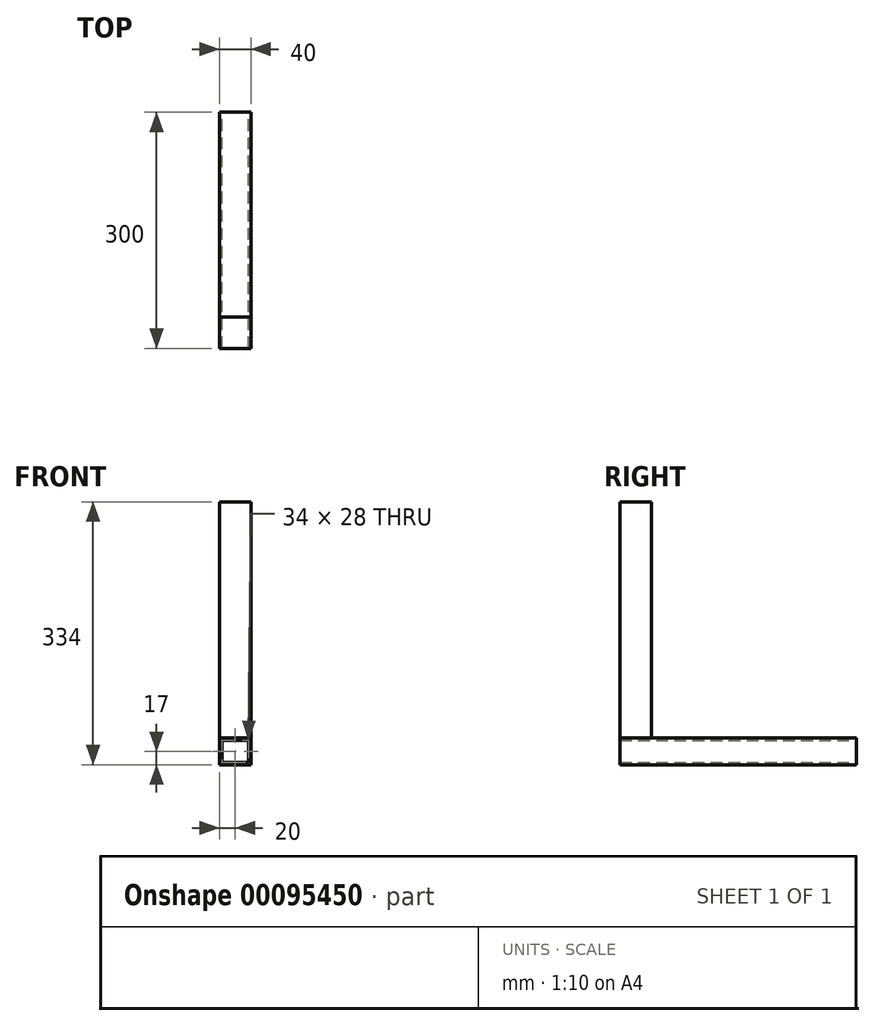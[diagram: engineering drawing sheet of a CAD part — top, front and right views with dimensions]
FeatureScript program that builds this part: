
annotation { "Feature Type Name" : "Feature", "Feature Type Description" : "" }
export const myFeature = defineFeature(function(context is Context, id is Id, definition is map)
    precondition{}
    {
        {
            var Q0;
            Q0=qCreatedBy(makeId("Front.planeOp"),FACE);
            var sketch = newSketch(context, id + "F0", { "sketchPlane" : qUnion([Q0])});
            skLineSegment(sketch, "E0.bottom", {"start": v(17, -14) * mm, "end": v(-17, -14) * mm});
            skLineSegment(sketch, "E0.top", {"start": v(17, 14) * mm, "end": v(-17, 14) * mm});
            skLineSegment(sketch, "E0.left", {"start": v(17, -14) * mm, "end": v(17, 14) * mm});
            skLineSegment(sketch, "E0.right", {"start": v(-17, -14) * mm, "end": v(-17, 14) * mm});
            skPoint(sketch, "E0.middle", {"position": v(0, 0) * mm});
            skLineSegment(sketch, "E1.bottom", {"start": v(20, -17) * mm, "end": v(-20, -17) * mm});
            skLineSegment(sketch, "E1.top", {"start": v(20, 17) * mm, "end": v(-20, 17) * mm});
            skLineSegment(sketch, "E1.left", {"start": v(20, -17) * mm, "end": v(20, 17) * mm});
            skLineSegment(sketch, "E1.right", {"start": v(-20, -17) * mm, "end": v(-20, 17) * mm});
            skSolve(sketch);
        }
        {
            var Q0;
            Q0 = qSketchRegion(id + "F0", true);
            extrude(context, id + "F1", {"entities" : qUnion([Q0]), "depth" : 300 * mm});
        }
        {
            var Q0;
            Q0=makeQuery(id+"F1.opExtrude","SWEPT_FACE",FACE,{"disambiguationData":[OSD([sQuery(id+"F0.wireOp",EDGE,"E1.top")])]});
            var sketch = newSketch(context, id + "F2", { "sketchPlane" : qUnion([Q0])});
            skLineSegment(sketch, "E2.bottom", {"start": v(20, -300) * mm, "end": v(-20, -300) * mm});
            skLineSegment(sketch, "E2.top", {"start": v(20, -260) * mm, "end": v(-20, -260) * mm});
            skLineSegment(sketch, "E2.left", {"start": v(20, -300) * mm, "end": v(20, -260) * mm});
            skLineSegment(sketch, "E2.right", {"start": v(-20, -300) * mm, "end": v(-20, -260) * mm});
            skSolve(sketch);
        }
        {
            var Q0;
            Q0 = qSketchRegion(id + "F2", true);
            extrude(context, id + "F3", {"entities" : qUnion([Q0]), "depth" : 300 * mm});
        }
    });
